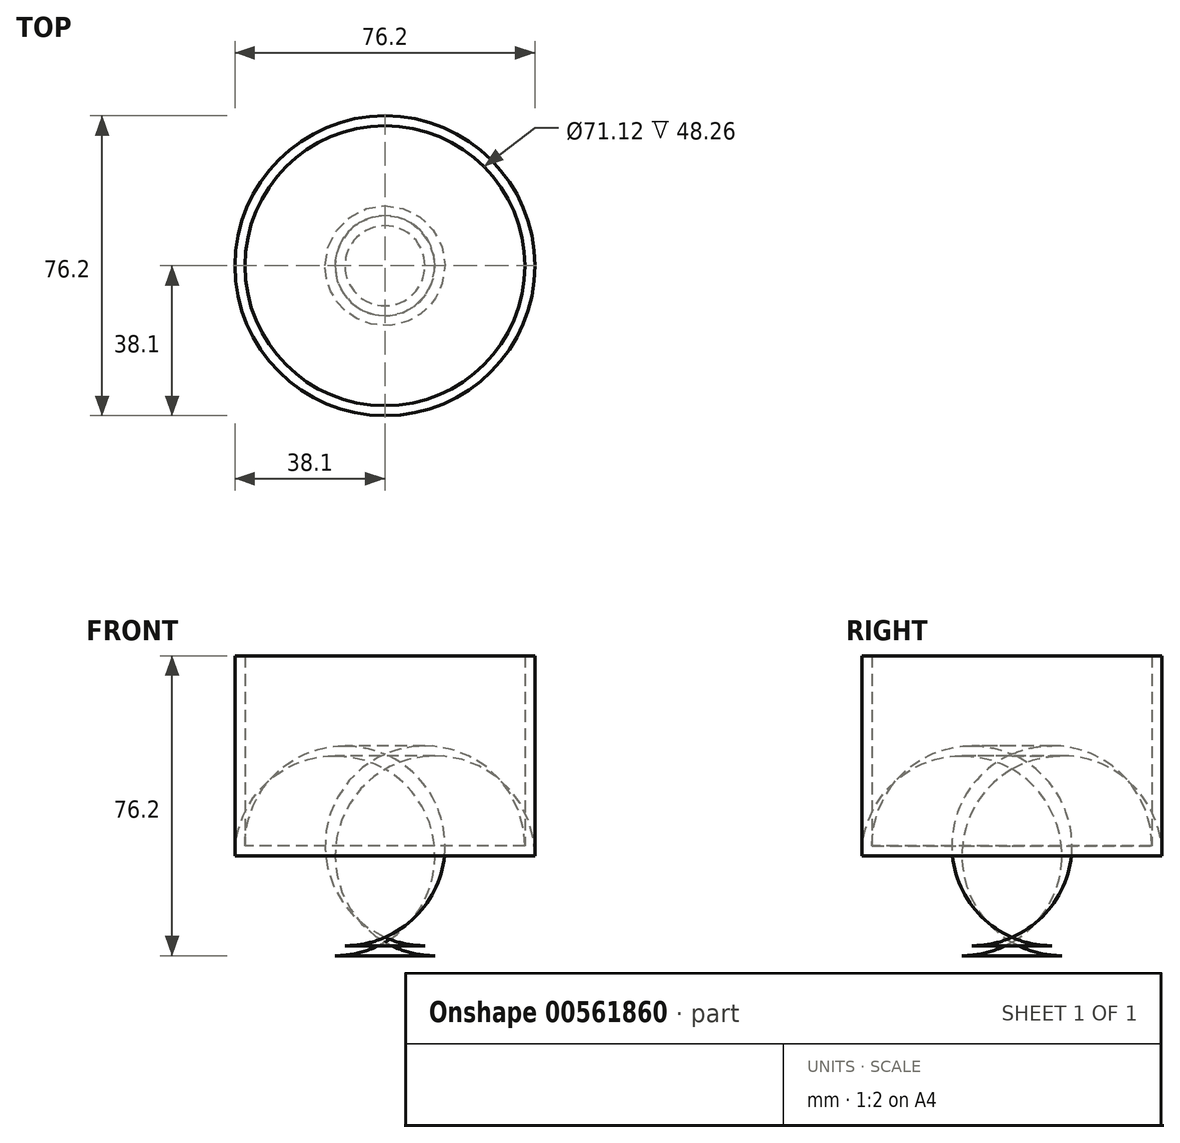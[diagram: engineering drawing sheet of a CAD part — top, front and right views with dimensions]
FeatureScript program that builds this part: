
annotation { "Feature Type Name" : "Feature", "Feature Type Description" : "" }
export const myFeature = defineFeature(function(context is Context, id is Id, definition is map)
    precondition{}
    {
        {
            var Q0;
            Q0=qCreatedBy(makeId("Top.planeOp"),FACE);
            var sketch = newSketch(context, id + "F0", { "sketchPlane" : qUnion([Q0])});
            skCircle(sketch, "E0", {"center": v(0, 0) * mm, "radius": 42.06 * mm});
            skSolve(sketch);
        }
        {
            var Q0;
            Q0=makeQuery(id+"F0.imprint","IMPRINT",FACE,{"disambiguationData":[TD([[makeQuery(id+"F0.imprint","IMPRINT",EDGE,{"derivedFrom":sQuery(id+"F0.wireOp",EDGE,"E0")}),1.0]])]});
            extrude(context, id + "F1", {"entities" : qUnion([Q0]), "depth" : 76.2 * mm, "offsetDistance" : 25.4 * mm});
        }
        {
            var Q0;
            Q0=makeQuery(id+"F1.opExtrude","CAP_FACE",FACE,{"disambiguationData":[OSD([sQuery(id+"F0.wireOp",EDGE,"E0")])],"isStart":false});
            shell(context, id + "F2", {"entities" : qUnion([Q0]), "thickness" : 2.54 * mm});
        }
        {
            var Q0;
            {var subQ0=sQuery(id+"F0.wireOp",EDGE,"E0");Q0=makeQuery(id+"F2.opShell","OFFSET_EDGE",EDGE,{"disambiguationData":[OSD([subQ0]),TDD([makeQuery(id+"F1.opExtrude","CAP_EDGE",EDGE,{"disambiguationData":[OSD([subQ0])],"isStart":true})])]});}
            var Q1;
            Q1=makeQuery(id+"F1.opExtrude","CAP_EDGE",EDGE,{"disambiguationData":[OSD([sQuery(id+"F0.wireOp",EDGE,"E0")])],"isStart":true});
            fillet(context, id + "F3", {"entities" : qUnion([Q0, Q1]), "radius" : 25.4 * mm, "tangentPropagation" : true, "allowEdgeOverflow" : false});
        }
        {
            var Q0;
            Q0=makeQuery(id+"F1.opExtrude","CAP_FACE",FACE,{"disambiguationData":[OSD([sQuery(id+"F0.wireOp",EDGE,"E0")])],"isStart":false});
            var sketch = newSketch(context, id + "F4", { "sketchPlane" : qUnion([Q0])});
            skCircle(sketch, "E1", {"center": v(0, 0) * mm, "radius": 42.06 * mm});
            skPoint(sketch, "E1.first.point", {"position": v(-36.23, -21.36) * mm});
            skPoint(sketch, "E1.second.point", {"position": v(35.6, 22.39) * mm});
            skPoint(sketch, "E1.third.point", {"position": v(16.13, -38.84) * mm});
            skSolve(sketch);
        }
        {
            var Q0;
            {var subQ0=sQuery(id+"F0.wireOp",EDGE,"E0");Q0=makeQuery(id+"F4.imprint","IMPRINT",FACE,{"disambiguationData":[TD([[makeQuery(id+"F4.imprint","IMPRINT",EDGE,{"derivedFrom":makeQuery(id+"F2.opShell","OFFSET_EDGE",EDGE,{"disambiguationData":[OSD([subQ0]),TDD([makeQuery(id+"F1.opExtrude","CAP_EDGE",EDGE,{"disambiguationData":[OSD([subQ0])],"isStart":false})])]})}),1.0]])]});}
            extrude(context, id + "F5", {"entities" : qUnion([Q0]), "depth" : 25.4 * mm, "offsetDistance" : 25.4 * mm});
        }
        {
            var Q0;
            Q0=makeQuery(id+"F5.opExtrude","SWEPT_BODY",BODY,{"disambiguationData":[OSD([sQuery(id+"F0.wireOp",EDGE,"E0")])]});
            deleteBodies(context, id + "F6", {"entities" : qUnion([Q0])});
        }
        {
            var Q0;
            Q0=makeQuery(id+"F1.opExtrude","SWEPT_BODY",BODY,{"disambiguationData":[OSD([sQuery(id+"F0.wireOp",EDGE,"E0")])]});
            deleteBodies(context, id + "F7", {"entities" : qUnion([Q0])});
        }
        {
            var Q0;
            Q0=qCreatedBy(makeId("Top.planeOp"),FACE);
            var sketch = newSketch(context, id + "F8", { "sketchPlane" : qUnion([Q0])});
            skCircle(sketch, "E2", {"center": v(0, 0) * mm, "radius": 38.1 * mm});
            skSolve(sketch);
        }
        {
            var Q0;
            Q0=makeQuery(id+"F8.imprint","IMPRINT",FACE,{"disambiguationData":[TD([[makeQuery(id+"F8.imprint","IMPRINT",EDGE,{"derivedFrom":sQuery(id+"F8.wireOp",EDGE,"E2")}),1.0]])]});
            extrude(context, id + "F9", {"entities" : qUnion([Q0]), "depth" : 76.2 * mm, "offsetDistance" : 25.4 * mm});
        }
        {
            var Q0;
            Q0=makeQuery(id+"F9.opExtrude","CAP_FACE",FACE,{"disambiguationData":[OSD([sQuery(id+"F8.wireOp",EDGE,"E2")])],"isStart":false});
            shell(context, id + "F10", {"entities" : qUnion([Q0]), "thickness" : 2.54 * mm});
        }
        {
            var Q0;
            {var subQ0=sQuery(id+"F8.wireOp",EDGE,"E2");Q0=makeQuery(id+"F10.opShell","OFFSET_EDGE",EDGE,{"disambiguationData":[OSD([subQ0]),TDD([makeQuery(id+"F9.opExtrude","CAP_EDGE",EDGE,{"disambiguationData":[OSD([subQ0])],"isStart":true})])]});}
            var Q1;
            Q1=makeQuery(id+"F9.opExtrude","CAP_EDGE",EDGE,{"disambiguationData":[OSD([sQuery(id+"F8.wireOp",EDGE,"E2")])],"isStart":true});
            fillet(context, id + "F11", {"entities" : qUnion([Q0, Q1]), "radius" : 25.4 * mm, "tangentPropagation" : true, "allowEdgeOverflow" : false});
        }
    });
